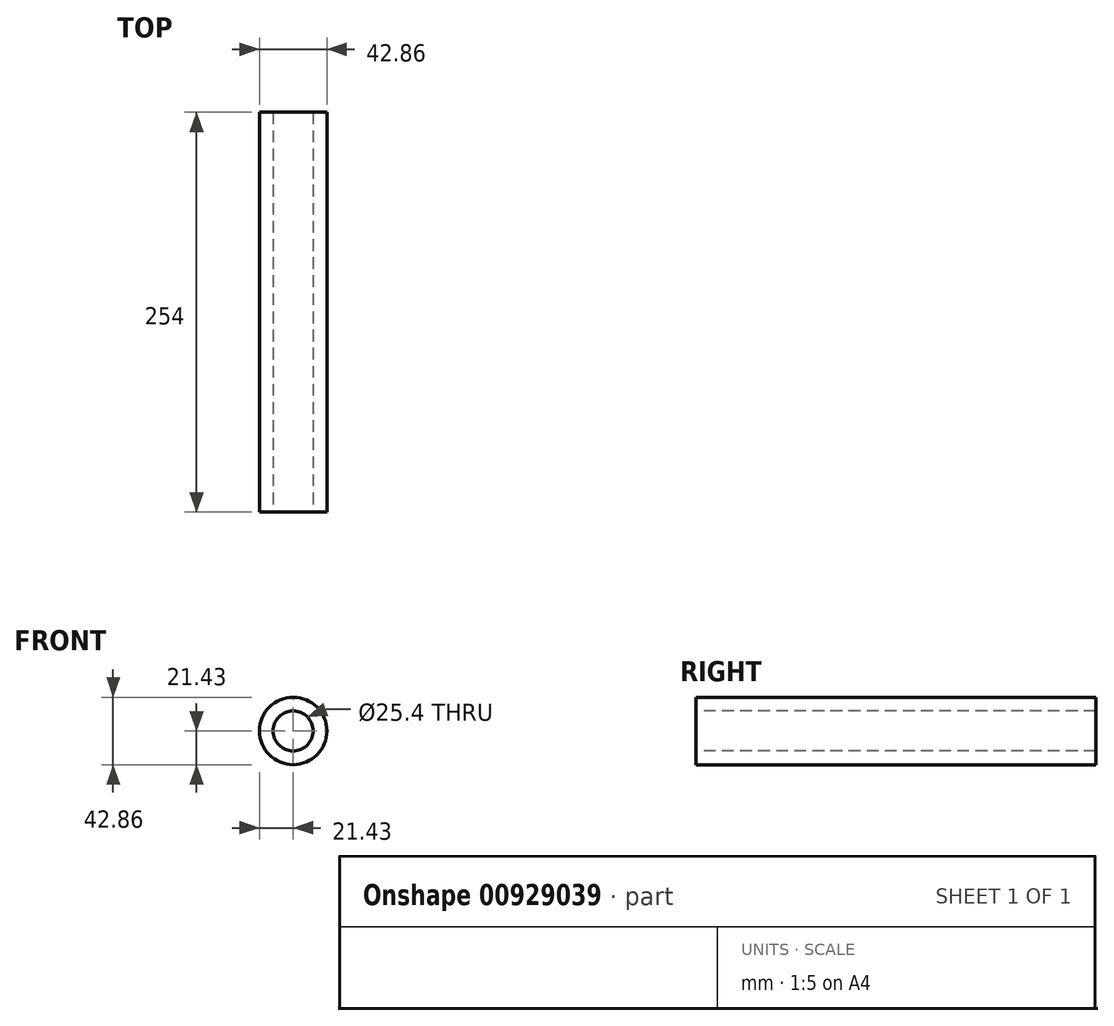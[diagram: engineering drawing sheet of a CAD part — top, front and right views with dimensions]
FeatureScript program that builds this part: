
annotation { "Feature Type Name" : "Feature", "Feature Type Description" : "" }
export const myFeature = defineFeature(function(context is Context, id is Id, definition is map)
    precondition{}
    {
        {
            var Q0;
            Q0=qCreatedBy(makeId("Front.planeOp"),FACE);
            var sketch = newSketch(context, id + "F0", { "sketchPlane" : qUnion([Q0])});
            skCircle(sketch, "E0", {"center": v(0, 0) * mm, "radius": 21.43 * mm});
            skCircle(sketch, "E1", {"center": v(0, 0) * mm, "radius": 12.7 * mm});
            skSolve(sketch);
        }
        {
            var Q0;
            Q0=makeQuery(id+"F0.imprint","IMPRINT",FACE,{"disambiguationData":[TD([[makeQuery(id+"F0.imprint","IMPRINT",EDGE,{"derivedFrom":sQuery(id+"F0.wireOp",EDGE,"E0")}),1.0]])]});
            extrude(context, id + "F1", {"entities" : qUnion([Q0]), "oppositeDirection" : true, "depth" : 254 * mm, "offsetDistance" : 25.4 * mm});
        }
    });
